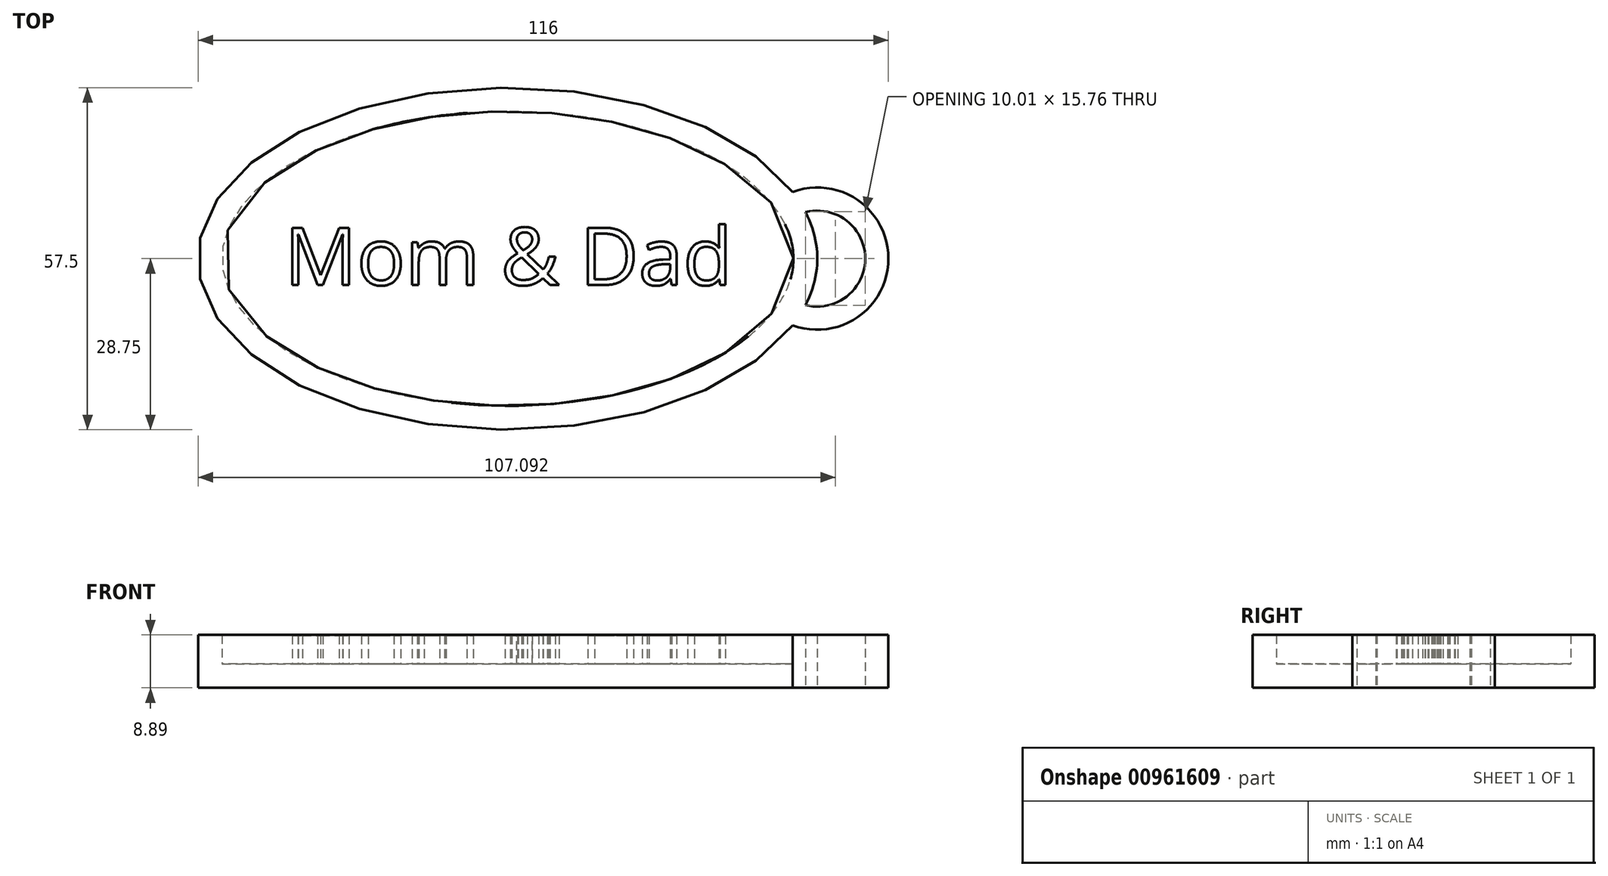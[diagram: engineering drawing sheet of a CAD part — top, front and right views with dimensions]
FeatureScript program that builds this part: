
annotation { "Feature Type Name" : "Feature", "Feature Type Description" : "" }
export const myFeature = defineFeature(function(context is Context, id is Id, definition is map)
    precondition{}
    {
        {
            var Q0;
            Q0=qCreatedBy(makeId("Top.planeOp"),FACE);
            var sketch = newSketch(context, id + "F0", { "sketchPlane" : qUnion([Q0])});
            skEllipticalArc(sketch, "E0", {});
            skArc(sketch, "E1", {"start": v(47.9, -11.22) * mm, "mid": v(63.98, 0) * mm, "end": v(47.9, 11.22) * mm});
            skArc(sketch, "E2", {"start": v(50.07, -7.81) * mm, "mid": v(60.08, 0) * mm, "end": v(50.07, 7.81) * mm});
            skEllipticalArc(sketch, "E3.trimOffspring", {});
            const initialGuessF0  = {"E0": [0, 0, -1, 0, 0.05202412637813248, 0.028745610506936522, 3.542674849956159, 2.7405104572234262], "E3.trimOffspring": [0, 0, -1, 0, 0.05202412637813248, 0.028745610506936522, 2.8663269902210695, 3.416858316958763]};
            skSetInitialGuess(sketch, initialGuessF0);
            skSolve(sketch);
        }
        {
            var Q0;
            Q0=makeQuery(id+"F0.imprint","IMPRINT",FACE,{"disambiguationData":[TD([[makeQuery(id+"F0.imprint","IMPRINT",EDGE,{"derivedFrom":sQuery(id+"F0.wireOp",EDGE,"E0")}),1.0]])]});
            extrude(context, id + "F1", {"entities" : qUnion([Q0]), "depth" : 8.9 * mm, "offsetDistance" : 25 * mm});
        }
        {
            var Q0;
            Q0=makeQuery(id+"F1.opExtrude","CAP_FACE",FACE,{"disambiguationData":[OSD([sQuery(id+"F0.wireOp",EDGE,"E0"),sQuery(id+"F0.wireOp",EDGE,"E1"),sQuery(id+"F0.wireOp",EDGE,"E2"),sQuery(id+"F0.wireOp",EDGE,"E3.trimOffspring"),sQuery(id+"F0.wireOp",EDGE,"9897f1b0-ff4b-4350-b235-9422b53804ee.sketch_text.stroke-0"),sQuery(id+"F0.wireOp",EDGE,"9897f1b0-ff4b-4350-b235-9422b53804ee.sketch_text.stroke-1"),sQuery(id+"F0.wireOp",EDGE,"9897f1b0-ff4b-4350-b235-9422b53804ee.sketch_text.stroke-2"),sQuery(id+"F0.wireOp",EDGE,"9897f1b0-ff4b-4350-b235-9422b53804ee.sketch_text.stroke-3"),sQuery(id+"F0.wireOp",EDGE,"9897f1b0-ff4b-4350-b235-9422b53804ee.sketch_text.stroke-4"),sQuery(id+"F0.wireOp",EDGE,"9897f1b0-ff4b-4350-b235-9422b53804ee.sketch_text.stroke-5"),sQuery(id+"F0.wireOp",EDGE,"9897f1b0-ff4b-4350-b235-9422b53804ee.sketch_text.stroke-6"),sQuery(id+"F0.wireOp",EDGE,"9897f1b0-ff4b-4350-b235-9422b53804ee.sketch_text.stroke-7"),sQuery(id+"F0.wireOp",EDGE,"9897f1b0-ff4b-4350-b235-9422b53804ee.sketch_text.stroke-8"),sQuery(id+"F0.wireOp",EDGE,"9897f1b0-ff4b-4350-b235-9422b53804ee.sketch_text.stroke-9"),sQuery(id+"F0.wireOp",EDGE,"9897f1b0-ff4b-4350-b235-9422b53804ee.sketch_text.stroke-10"),sQuery(id+"F0.wireOp",EDGE,"9897f1b0-ff4b-4350-b235-9422b53804ee.sketch_text.stroke-11"),sQuery(id+"F0.wireOp",EDGE,"9897f1b0-ff4b-4350-b235-9422b53804ee.sketch_text.stroke-12"),sQuery(id+"F0.wireOp",EDGE,"9897f1b0-ff4b-4350-b235-9422b53804ee.sketch_text.stroke-13"),sQuery(id+"F0.wireOp",EDGE,"9897f1b0-ff4b-4350-b235-9422b53804ee.sketch_text.stroke-14"),sQuery(id+"F0.wireOp",EDGE,"9897f1b0-ff4b-4350-b235-9422b53804ee.sketch_text.stroke-15"),sQuery(id+"F0.wireOp",EDGE,"9897f1b0-ff4b-4350-b235-9422b53804ee.sketch_text.stroke-16"),sQuery(id+"F0.wireOp",EDGE,"9897f1b0-ff4b-4350-b235-9422b53804ee.sketch_text.stroke-17"),sQuery(id+"F0.wireOp",EDGE,"9897f1b0-ff4b-4350-b235-9422b53804ee.sketch_text.stroke-18"),sQuery(id+"F0.wireOp",EDGE,"9897f1b0-ff4b-4350-b235-9422b53804ee.sketch_text.stroke-19"),sQuery(id+"F0.wireOp",EDGE,"9897f1b0-ff4b-4350-b235-9422b53804ee.sketch_text.stroke-20"),sQuery(id+"F0.wireOp",EDGE,"9897f1b0-ff4b-4350-b235-9422b53804ee.sketch_text.stroke-21"),sQuery(id+"F0.wireOp",EDGE,"9897f1b0-ff4b-4350-b235-9422b53804ee.sketch_text.stroke-22"),sQuery(id+"F0.wireOp",EDGE,"9897f1b0-ff4b-4350-b235-9422b53804ee.sketch_text.stroke-23"),sQuery(id+"F0.wireOp",EDGE,"9897f1b0-ff4b-4350-b235-9422b53804ee.sketch_text.stroke-24"),sQuery(id+"F0.wireOp",EDGE,"9897f1b0-ff4b-4350-b235-9422b53804ee.sketch_text.stroke-25"),sQuery(id+"F0.wireOp",EDGE,"9897f1b0-ff4b-4350-b235-9422b53804ee.sketch_text.stroke-26"),sQuery(id+"F0.wireOp",EDGE,"9897f1b0-ff4b-4350-b235-9422b53804ee.sketch_text.stroke-35"),sQuery(id+"F0.wireOp",EDGE,"9897f1b0-ff4b-4350-b235-9422b53804ee.sketch_text.stroke-36"),sQuery(id+"F0.wireOp",EDGE,"9897f1b0-ff4b-4350-b235-9422b53804ee.sketch_text.stroke-37"),sQuery(id+"F0.wireOp",EDGE,"9897f1b0-ff4b-4350-b235-9422b53804ee.sketch_text.stroke-38"),sQuery(id+"F0.wireOp",EDGE,"9897f1b0-ff4b-4350-b235-9422b53804ee.sketch_text.stroke-39"),sQuery(id+"F0.wireOp",EDGE,"9897f1b0-ff4b-4350-b235-9422b53804ee.sketch_text.stroke-40"),sQuery(id+"F0.wireOp",EDGE,"9897f1b0-ff4b-4350-b235-9422b53804ee.sketch_text.stroke-41"),sQuery(id+"F0.wireOp",EDGE,"9897f1b0-ff4b-4350-b235-9422b53804ee.sketch_text.stroke-42"),sQuery(id+"F0.wireOp",EDGE,"9897f1b0-ff4b-4350-b235-9422b53804ee.sketch_text.stroke-43"),sQuery(id+"F0.wireOp",EDGE,"9897f1b0-ff4b-4350-b235-9422b53804ee.sketch_text.stroke-44"),sQuery(id+"F0.wireOp",EDGE,"9897f1b0-ff4b-4350-b235-9422b53804ee.sketch_text.stroke-45"),sQuery(id+"F0.wireOp",EDGE,"9897f1b0-ff4b-4350-b235-9422b53804ee.sketch_text.stroke-46"),sQuery(id+"F0.wireOp",EDGE,"9897f1b0-ff4b-4350-b235-9422b53804ee.sketch_text.stroke-47"),sQuery(id+"F0.wireOp",EDGE,"9897f1b0-ff4b-4350-b235-9422b53804ee.sketch_text.stroke-48"),sQuery(id+"F0.wireOp",EDGE,"9897f1b0-ff4b-4350-b235-9422b53804ee.sketch_text.stroke-49"),sQuery(id+"F0.wireOp",EDGE,"9897f1b0-ff4b-4350-b235-9422b53804ee.sketch_text.stroke-50"),sQuery(id+"F0.wireOp",EDGE,"9897f1b0-ff4b-4350-b235-9422b53804ee.sketch_text.stroke-51"),sQuery(id+"F0.wireOp",EDGE,"9897f1b0-ff4b-4350-b235-9422b53804ee.sketch_text.stroke-52"),sQuery(id+"F0.wireOp",EDGE,"9897f1b0-ff4b-4350-b235-9422b53804ee.sketch_text.stroke-53"),sQuery(id+"F0.wireOp",EDGE,"9897f1b0-ff4b-4350-b235-9422b53804ee.sketch_text.stroke-54"),sQuery(id+"F0.wireOp",EDGE,"9897f1b0-ff4b-4350-b235-9422b53804ee.sketch_text.stroke-55"),sQuery(id+"F0.wireOp",EDGE,"9897f1b0-ff4b-4350-b235-9422b53804ee.sketch_text.stroke-56"),sQuery(id+"F0.wireOp",EDGE,"9897f1b0-ff4b-4350-b235-9422b53804ee.sketch_text.stroke-57"),sQuery(id+"F0.wireOp",EDGE,"9897f1b0-ff4b-4350-b235-9422b53804ee.sketch_text.stroke-58"),sQuery(id+"F0.wireOp",EDGE,"9897f1b0-ff4b-4350-b235-9422b53804ee.sketch_text.stroke-59"),sQuery(id+"F0.wireOp",EDGE,"9897f1b0-ff4b-4350-b235-9422b53804ee.sketch_text.stroke-60"),sQuery(id+"F0.wireOp",EDGE,"9897f1b0-ff4b-4350-b235-9422b53804ee.sketch_text.stroke-61"),sQuery(id+"F0.wireOp",EDGE,"9897f1b0-ff4b-4350-b235-9422b53804ee.sketch_text.stroke-62"),sQuery(id+"F0.wireOp",EDGE,"9897f1b0-ff4b-4350-b235-9422b53804ee.sketch_text.stroke-78"),sQuery(id+"F0.wireOp",EDGE,"9897f1b0-ff4b-4350-b235-9422b53804ee.sketch_text.stroke-79"),sQuery(id+"F0.wireOp",EDGE,"9897f1b0-ff4b-4350-b235-9422b53804ee.sketch_text.stroke-80"),sQuery(id+"F0.wireOp",EDGE,"9897f1b0-ff4b-4350-b235-9422b53804ee.sketch_text.stroke-81"),sQuery(id+"F0.wireOp",EDGE,"9897f1b0-ff4b-4350-b235-9422b53804ee.sketch_text.stroke-82"),sQuery(id+"F0.wireOp",EDGE,"9897f1b0-ff4b-4350-b235-9422b53804ee.sketch_text.stroke-83"),sQuery(id+"F0.wireOp",EDGE,"9897f1b0-ff4b-4350-b235-9422b53804ee.sketch_text.stroke-84"),sQuery(id+"F0.wireOp",EDGE,"9897f1b0-ff4b-4350-b235-9422b53804ee.sketch_text.stroke-85"),sQuery(id+"F0.wireOp",EDGE,"9897f1b0-ff4b-4350-b235-9422b53804ee.sketch_text.stroke-86"),sQuery(id+"F0.wireOp",EDGE,"9897f1b0-ff4b-4350-b235-9422b53804ee.sketch_text.stroke-87"),sQuery(id+"F0.wireOp",EDGE,"9897f1b0-ff4b-4350-b235-9422b53804ee.sketch_text.stroke-88"),sQuery(id+"F0.wireOp",EDGE,"9897f1b0-ff4b-4350-b235-9422b53804ee.sketch_text.stroke-89"),sQuery(id+"F0.wireOp",EDGE,"9897f1b0-ff4b-4350-b235-9422b53804ee.sketch_text.stroke-90"),sQuery(id+"F0.wireOp",EDGE,"9897f1b0-ff4b-4350-b235-9422b53804ee.sketch_text.stroke-91"),sQuery(id+"F0.wireOp",EDGE,"9897f1b0-ff4b-4350-b235-9422b53804ee.sketch_text.stroke-92"),sQuery(id+"F0.wireOp",EDGE,"9897f1b0-ff4b-4350-b235-9422b53804ee.sketch_text.stroke-93"),sQuery(id+"F0.wireOp",EDGE,"9897f1b0-ff4b-4350-b235-9422b53804ee.sketch_text.stroke-94"),sQuery(id+"F0.wireOp",EDGE,"9897f1b0-ff4b-4350-b235-9422b53804ee.sketch_text.stroke-95"),sQuery(id+"F0.wireOp",EDGE,"9897f1b0-ff4b-4350-b235-9422b53804ee.sketch_text.stroke-96"),sQuery(id+"F0.wireOp",EDGE,"9897f1b0-ff4b-4350-b235-9422b53804ee.sketch_text.stroke-97"),sQuery(id+"F0.wireOp",EDGE,"9897f1b0-ff4b-4350-b235-9422b53804ee.sketch_text.stroke-98"),sQuery(id+"F0.wireOp",EDGE,"9897f1b0-ff4b-4350-b235-9422b53804ee.sketch_text.stroke-99"),sQuery(id+"F0.wireOp",EDGE,"9897f1b0-ff4b-4350-b235-9422b53804ee.sketch_text.stroke-100"),sQuery(id+"F0.wireOp",EDGE,"9897f1b0-ff4b-4350-b235-9422b53804ee.sketch_text.stroke-101"),sQuery(id+"F0.wireOp",EDGE,"9897f1b0-ff4b-4350-b235-9422b53804ee.sketch_text.stroke-102"),sQuery(id+"F0.wireOp",EDGE,"9897f1b0-ff4b-4350-b235-9422b53804ee.sketch_text.stroke-103"),sQuery(id+"F0.wireOp",EDGE,"9897f1b0-ff4b-4350-b235-9422b53804ee.sketch_text.stroke-104"),sQuery(id+"F0.wireOp",EDGE,"9897f1b0-ff4b-4350-b235-9422b53804ee.sketch_text.stroke-105"),sQuery(id+"F0.wireOp",EDGE,"9897f1b0-ff4b-4350-b235-9422b53804ee.sketch_text.stroke-106"),sQuery(id+"F0.wireOp",EDGE,"9897f1b0-ff4b-4350-b235-9422b53804ee.sketch_text.stroke-107"),sQuery(id+"F0.wireOp",EDGE,"9897f1b0-ff4b-4350-b235-9422b53804ee.sketch_text.stroke-115"),sQuery(id+"F0.wireOp",EDGE,"9897f1b0-ff4b-4350-b235-9422b53804ee.sketch_text.stroke-116"),sQuery(id+"F0.wireOp",EDGE,"9897f1b0-ff4b-4350-b235-9422b53804ee.sketch_text.stroke-117"),sQuery(id+"F0.wireOp",EDGE,"9897f1b0-ff4b-4350-b235-9422b53804ee.sketch_text.stroke-118"),sQuery(id+"F0.wireOp",EDGE,"9897f1b0-ff4b-4350-b235-9422b53804ee.sketch_text.stroke-119"),sQuery(id+"F0.wireOp",EDGE,"9897f1b0-ff4b-4350-b235-9422b53804ee.sketch_text.stroke-120"),sQuery(id+"F0.wireOp",EDGE,"9897f1b0-ff4b-4350-b235-9422b53804ee.sketch_text.stroke-121"),sQuery(id+"F0.wireOp",EDGE,"9897f1b0-ff4b-4350-b235-9422b53804ee.sketch_text.stroke-122"),sQuery(id+"F0.wireOp",EDGE,"9897f1b0-ff4b-4350-b235-9422b53804ee.sketch_text.stroke-123"),sQuery(id+"F0.wireOp",EDGE,"9897f1b0-ff4b-4350-b235-9422b53804ee.sketch_text.stroke-124"),sQuery(id+"F0.wireOp",EDGE,"9897f1b0-ff4b-4350-b235-9422b53804ee.sketch_text.stroke-125"),sQuery(id+"F0.wireOp",EDGE,"9897f1b0-ff4b-4350-b235-9422b53804ee.sketch_text.stroke-126"),sQuery(id+"F0.wireOp",EDGE,"9897f1b0-ff4b-4350-b235-9422b53804ee.sketch_text.stroke-127"),sQuery(id+"F0.wireOp",EDGE,"9897f1b0-ff4b-4350-b235-9422b53804ee.sketch_text.stroke-128"),sQuery(id+"F0.wireOp",EDGE,"9897f1b0-ff4b-4350-b235-9422b53804ee.sketch_text.stroke-129"),sQuery(id+"F0.wireOp",EDGE,"9897f1b0-ff4b-4350-b235-9422b53804ee.sketch_text.stroke-130"),sQuery(id+"F0.wireOp",EDGE,"9897f1b0-ff4b-4350-b235-9422b53804ee.sketch_text.stroke-131"),sQuery(id+"F0.wireOp",EDGE,"9897f1b0-ff4b-4350-b235-9422b53804ee.sketch_text.stroke-132"),sQuery(id+"F0.wireOp",EDGE,"9897f1b0-ff4b-4350-b235-9422b53804ee.sketch_text.stroke-133"),sQuery(id+"F0.wireOp",EDGE,"9897f1b0-ff4b-4350-b235-9422b53804ee.sketch_text.stroke-142"),sQuery(id+"F0.wireOp",EDGE,"9897f1b0-ff4b-4350-b235-9422b53804ee.sketch_text.stroke-143"),sQuery(id+"F0.wireOp",EDGE,"9897f1b0-ff4b-4350-b235-9422b53804ee.sketch_text.stroke-144"),sQuery(id+"F0.wireOp",EDGE,"9897f1b0-ff4b-4350-b235-9422b53804ee.sketch_text.stroke-145"),sQuery(id+"F0.wireOp",EDGE,"9897f1b0-ff4b-4350-b235-9422b53804ee.sketch_text.stroke-146"),sQuery(id+"F0.wireOp",EDGE,"9897f1b0-ff4b-4350-b235-9422b53804ee.sketch_text.stroke-147"),sQuery(id+"F0.wireOp",EDGE,"9897f1b0-ff4b-4350-b235-9422b53804ee.sketch_text.stroke-148"),sQuery(id+"F0.wireOp",EDGE,"9897f1b0-ff4b-4350-b235-9422b53804ee.sketch_text.stroke-149"),sQuery(id+"F0.wireOp",EDGE,"9897f1b0-ff4b-4350-b235-9422b53804ee.sketch_text.stroke-150"),sQuery(id+"F0.wireOp",EDGE,"9897f1b0-ff4b-4350-b235-9422b53804ee.sketch_text.stroke-151"),sQuery(id+"F0.wireOp",EDGE,"9897f1b0-ff4b-4350-b235-9422b53804ee.sketch_text.stroke-152"),sQuery(id+"F0.wireOp",EDGE,"9897f1b0-ff4b-4350-b235-9422b53804ee.sketch_text.stroke-153"),sQuery(id+"F0.wireOp",EDGE,"9897f1b0-ff4b-4350-b235-9422b53804ee.sketch_text.stroke-154"),sQuery(id+"F0.wireOp",EDGE,"9897f1b0-ff4b-4350-b235-9422b53804ee.sketch_text.stroke-155"),sQuery(id+"F0.wireOp",EDGE,"9897f1b0-ff4b-4350-b235-9422b53804ee.sketch_text.stroke-156")])],"isStart":false});
            shell(context, id + "F2", {"entities" : qUnion([Q0]), "thickness" : 4 * mm});
        }
        {
            var Q0;
            Q0=makeQuery(id+"F2.opShell","OFFSET_FACE",FACE,{"disambiguationData":[OSD([sQuery(id+"F0.wireOp",EDGE,"E0"),sQuery(id+"F0.wireOp",EDGE,"E1"),sQuery(id+"F0.wireOp",EDGE,"E2"),sQuery(id+"F0.wireOp",EDGE,"E3.trimOffspring")])]});
            var sketch = newSketch(context, id + "F3", { "sketchPlane" : qUnion([Q0])});
            skText(sketch, "E4", { "text": "Mom & Dad", "fontName": "OpenSans-Regular.ttf"});
            const initialGuessF3  = {"E4": [-0.0375, -0.00445, 1, 0, 0.0097]};
            skSetInitialGuess(sketch, initialGuessF3);
            skSolve(sketch);
        }
        {
            var Q0;
            Q0 = qSketchRegion(id + "F3", true);
            extrude(context, id + "F4", {"entities" : qUnion([Q0]), "operationType" : NewBodyOperationType.ADD, "depth" : 4.8 * mm, "offsetDistance" : 25 * mm});
        }
    });
